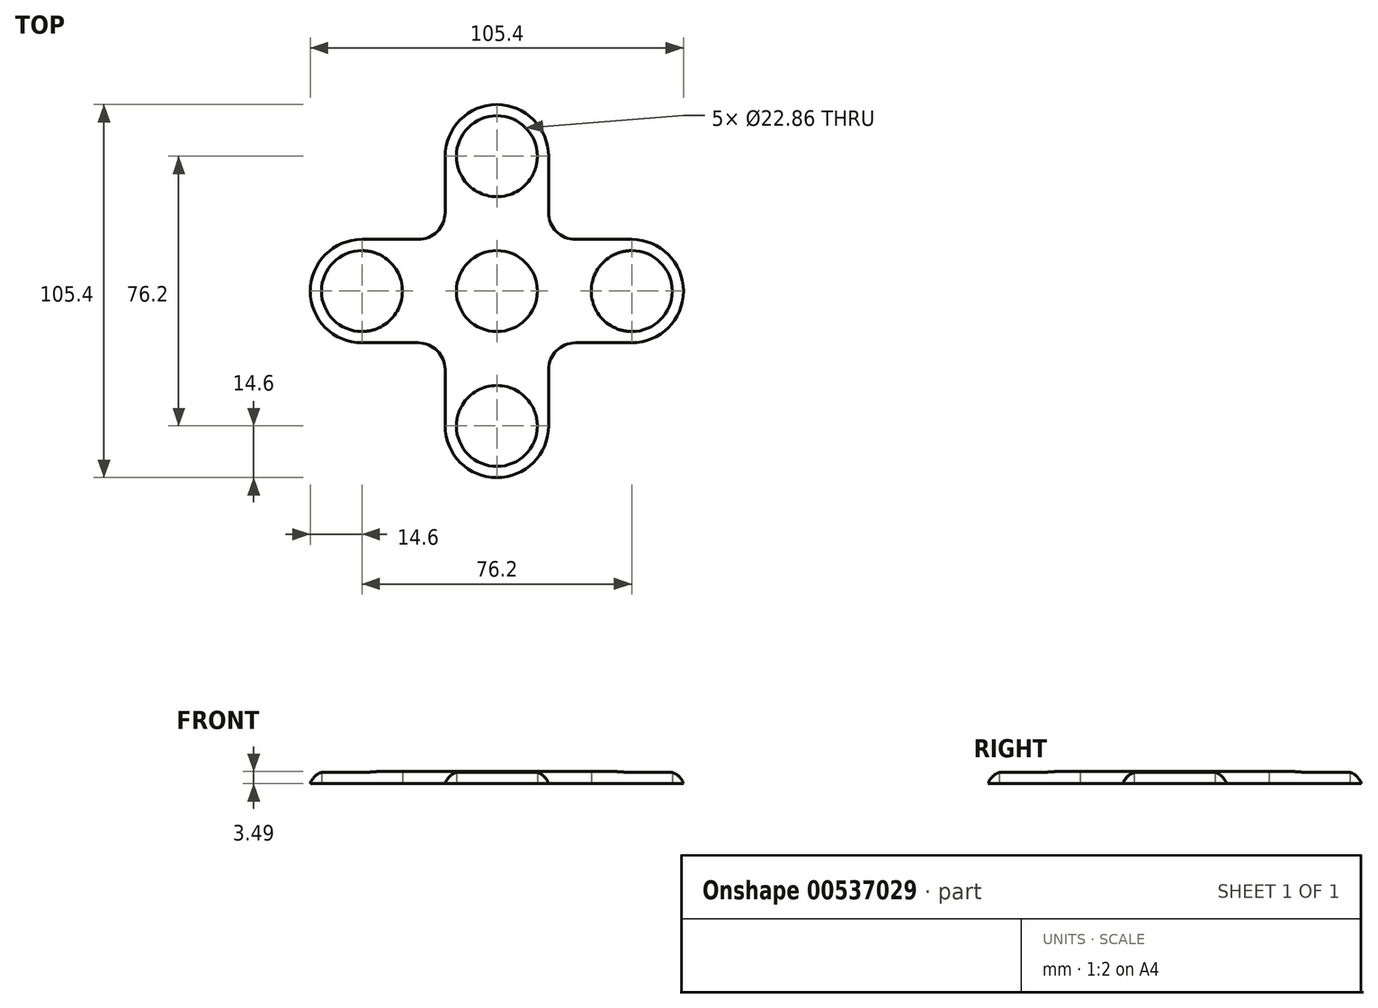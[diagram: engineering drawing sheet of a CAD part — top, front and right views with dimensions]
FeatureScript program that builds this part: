
annotation { "Feature Type Name" : "Feature", "Feature Type Description" : "" }
export const myFeature = defineFeature(function(context is Context, id is Id, definition is map)
    precondition{}
    {
        {
            var Q0;
            Q0=qCreatedBy(makeId("Top.planeOp"),FACE);
            var sketch = newSketch(context, id + "F0", { "sketchPlane" : qUnion([Q0])});
            skCircle(sketch, "E0", {"center": v(0, 0) * mm, "radius": 11.43 * mm});
            skCircle(sketch, "E1.0", {"center": v(0, 0) * mm, "radius": 14.6 * mm});
            skCircle(sketch, "E2", {"center": v(0, 38.1) * mm, "radius": 11.43 * mm});
            skCircle(sketch, "E3", {"center": v(0, 38.1) * mm, "radius": 14.6 * mm});
            skLineSegment(sketch, "E4", {"start": v(14.6, 38.1) * mm, "end": v(14.6, 22.22) * mm});
            skLineSegment(sketch, "E5", {"start": v(-14.6, 38.1) * mm, "end": v(-14.6, 22.22) * mm});
            skLineSegment(sketch, "E6.1.0", {"start": v(-38.1, -14.6) * mm, "end": v(-22.22, -14.6) * mm});
            skCircle(sketch, "E6.1.1", {"center": v(-38.1, 0) * mm, "radius": 14.6 * mm});
            skCircle(sketch, "E6.1.2", {"center": v(-38.1, 0) * mm, "radius": 11.43 * mm});
            skLineSegment(sketch, "E6.1.3", {"start": v(-38.1, 14.6) * mm, "end": v(-22.22, 14.6) * mm});
            skLineSegment(sketch, "E6.2.0", {"start": v(14.6, -38.1) * mm, "end": v(14.6, -22.23) * mm});
            skCircle(sketch, "E6.2.1", {"center": v(0, -38.1) * mm, "radius": 14.6 * mm});
            skCircle(sketch, "E6.2.2", {"center": v(0, -38.1) * mm, "radius": 11.43 * mm});
            skLineSegment(sketch, "E6.2.3", {"start": v(-14.6, -38.1) * mm, "end": v(-14.6, -22.23) * mm});
            skLineSegment(sketch, "E6.3.0", {"start": v(38.1, 14.6) * mm, "end": v(22.22, 14.6) * mm});
            skCircle(sketch, "E6.3.1", {"center": v(38.1, 0) * mm, "radius": 14.6 * mm});
            skCircle(sketch, "E6.3.2", {"center": v(38.1, 0) * mm, "radius": 11.43 * mm});
            skLineSegment(sketch, "E6.3.3", {"start": v(38.1, -14.6) * mm, "end": v(22.22, -14.6) * mm});
            skPoint(sketch, "E7.newPointA", {"position": v(0, 14.6) * mm});
            skPoint(sketch, "E7.newPointB", {"position": v(14.6, 0) * mm});
            skArc(sketch, "E7.filletArc", {"start": v(14.6, 22.22) * mm, "mid": v(16.84, 16.84) * mm, "end": v(22.22, 14.6) * mm});
            skPoint(sketch, "E8.newPointA", {"position": v(-14.6, 0) * mm});
            skArc(sketch, "E8.filletArc", {"start": v(-22.22, 14.6) * mm, "mid": v(-16.84, 16.84) * mm, "end": v(-14.6, 22.22) * mm});
            skPoint(sketch, "E9.newPointB", {"position": v(0, -14.6) * mm});
            skArc(sketch, "E9.filletArc", {"start": v(-14.6, -22.23) * mm, "mid": v(-16.84, -16.84) * mm, "end": v(-22.22, -14.6) * mm});
            skArc(sketch, "E10.filletArc", {"start": v(22.22, -14.6) * mm, "mid": v(16.84, -16.84) * mm, "end": v(14.6, -22.23) * mm});
            skLineSegment(sketch, "E11", {"start": v(0, 0) * mm, "end": v(-10.33, 10.33) * mm, "construction": true});
            skLineSegment(sketch, "E12.1.0", {"start": v(0, 0) * mm, "end": v(-10.33, -10.33) * mm, "construction": true});
            skLineSegment(sketch, "E12.2.0", {"start": v(0, 0) * mm, "end": v(10.33, -10.33) * mm, "construction": true});
            skLineSegment(sketch, "E12.3.0", {"start": v(0, 0) * mm, "end": v(10.33, 10.33) * mm, "construction": true});
            skSolve(sketch);
        }
        {
            var Q0;
            Q0 = qSketchRegion(id + "F0", true);
            var Q1;
            Q1=makeQuery(id+"F0.imprint","IMPRINT",FACE,{"disambiguationData":[TD([[makeQuery(id+"F0.imprint","IMPRINT",EDGE,{"derivedFrom":sQuery(id+"F0.wireOp",EDGE,"E0")}),-1.0]])]});
            extrude(context, id + "F1", {"entities" : qUnion([Q0, Q1]), "depth" : 3.5 * mm, "offsetDistance" : 25.4 * mm});
        }
        {
            var Q0;
            Q0=makeQuery(id+"F1.opExtrude","CAP_EDGE",EDGE,{"disambiguationData":[OSD([sQuery(id+"F0.wireOp",EDGE,"E6.2.1")])],"isStart":false});
            fillet(context, id + "F2", {"entities" : qUnion([Q0]), "radius" : 5.08 * mm, "tangentPropagation" : true, "allowEdgeOverflow" : false});
        }
    });
